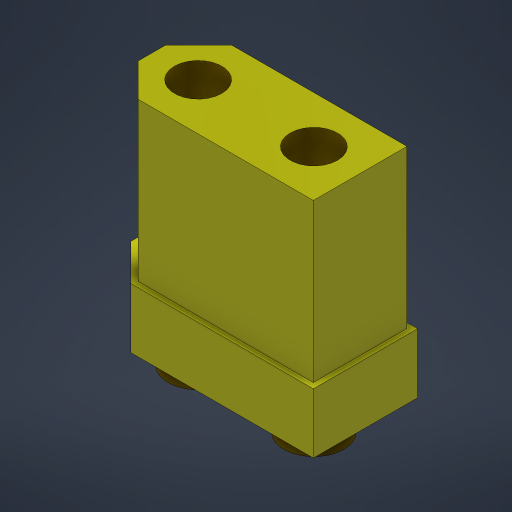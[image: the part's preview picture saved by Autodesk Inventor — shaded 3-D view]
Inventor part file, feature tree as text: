
AUTODESK INVENTOR PART (.ipt)
format: ipt  version: 2023.5 (Build 275446000, 446)  size: 205,312 bytes
history: native  units: mm
features: extrude x3, sketch x1
ambient origin geometry x8: Origin, YZ Plane, XZ Plane, XY Plane, X Axis, Y Axis, Z Axis, Center Point
bodies: Volumenkörper1 (feature_tree)
feature tree (4):
  sketch  "Skizze1"  dims[d2=20.8mm d4=45.0deg d5=9.9mm d6=3.0mm d8=5.7mm d9=11.0mm d11=4.9mm d12=0.5mm d13=4.5mm d14=20.7mm d15=0.0mm d16=23.5mm d17=0.0mm d18=15.0mm d19=0.0mm]
  extrude  "Extrusion1"  TaperAngle=45.0deg  [1 undecoded]
  extrude  "Extrusion2"  Depth=9.9mm
  extrude  "Extrusion3"  Depth=15.0mm
note: 1 required parameter value undecoded (feature->parameter linkage not recoverable at this tier; creation-order binding heuristic only, values carry confidence <= 0.55)
